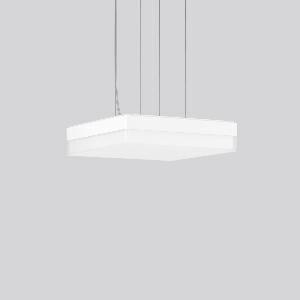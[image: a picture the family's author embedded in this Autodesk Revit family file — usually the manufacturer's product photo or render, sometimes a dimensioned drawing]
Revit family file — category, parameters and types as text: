
# Revit family: flat_slim_square_312541_002_730_d66b
name_source: partatom
category: Lighting Fixtures
units: mm (PartAtom-declared; Revit-internal decimal feet)

## family parameters
Cut with Voids When Loaded = No
Host = Face
Light Source = No
Part Type = Normal
Room Calculation Point = No
Round Connector Dimension = Use Diameter
Shared = No

## types (1)
- MultiLumen 2 840 (1 x LED Modul 840, 2400 lm, 4000)
    Apparent Load = 21 VA
    CIE Flux Codes = 43 74 93 92 100
    Color Rendering = 80
    Color Temperature = 4000
    Default Elevation = 1800 mm
    Height = 70 mm
    Lamp = 1 x LED Modul 840
    Lamp Light Flux = 2400 lm
    Lamp count = 1
    Length = 300 mm
    Lifetime = 50000 h
    Luminous efficacy = 114 lm/W
    Manufacturer = RZB
    ModVariant = No
    Model = 312541.002.730
    Mounting Place = Ceiling
    Mounting Type = Pendant
    Number of Poles = 1
    OnlyDefault = Yes
    Power Factor = 1
    Product Name = FLAT SLIM square
    Product group = Pendant luminaires
    ProductGroupID = 902
    Protection Class = Protection class I
    Protection Degree = IP 40
    RLX_Detail_Level = 1
    RLX_Emergency_Light_Flux = 0 lm
    RLX_Emergency_Type = 0
    RLX_Emergency_Type_DB = No
    RlxData = <blob elided: 14441 chars, md5=7e9e567f>
    Socket = socket
    Standby Power = 0 W
    System Light Flux = 2400 lm
    System Power = 21 W
    Type Comments = MultiLumen 2 840
    Type Image = 312541.002.jpg
    URL = http://relux.com
    VarID = multilumen_2_840
    Voltage = 230 V
    Voltage Range = 220-240 V
    Weight = 0.00 kg
    Width = 300 mm

## geometry (parser evidence)
native form markers: Sweep x13
no freeform markers — native parametric forms only
